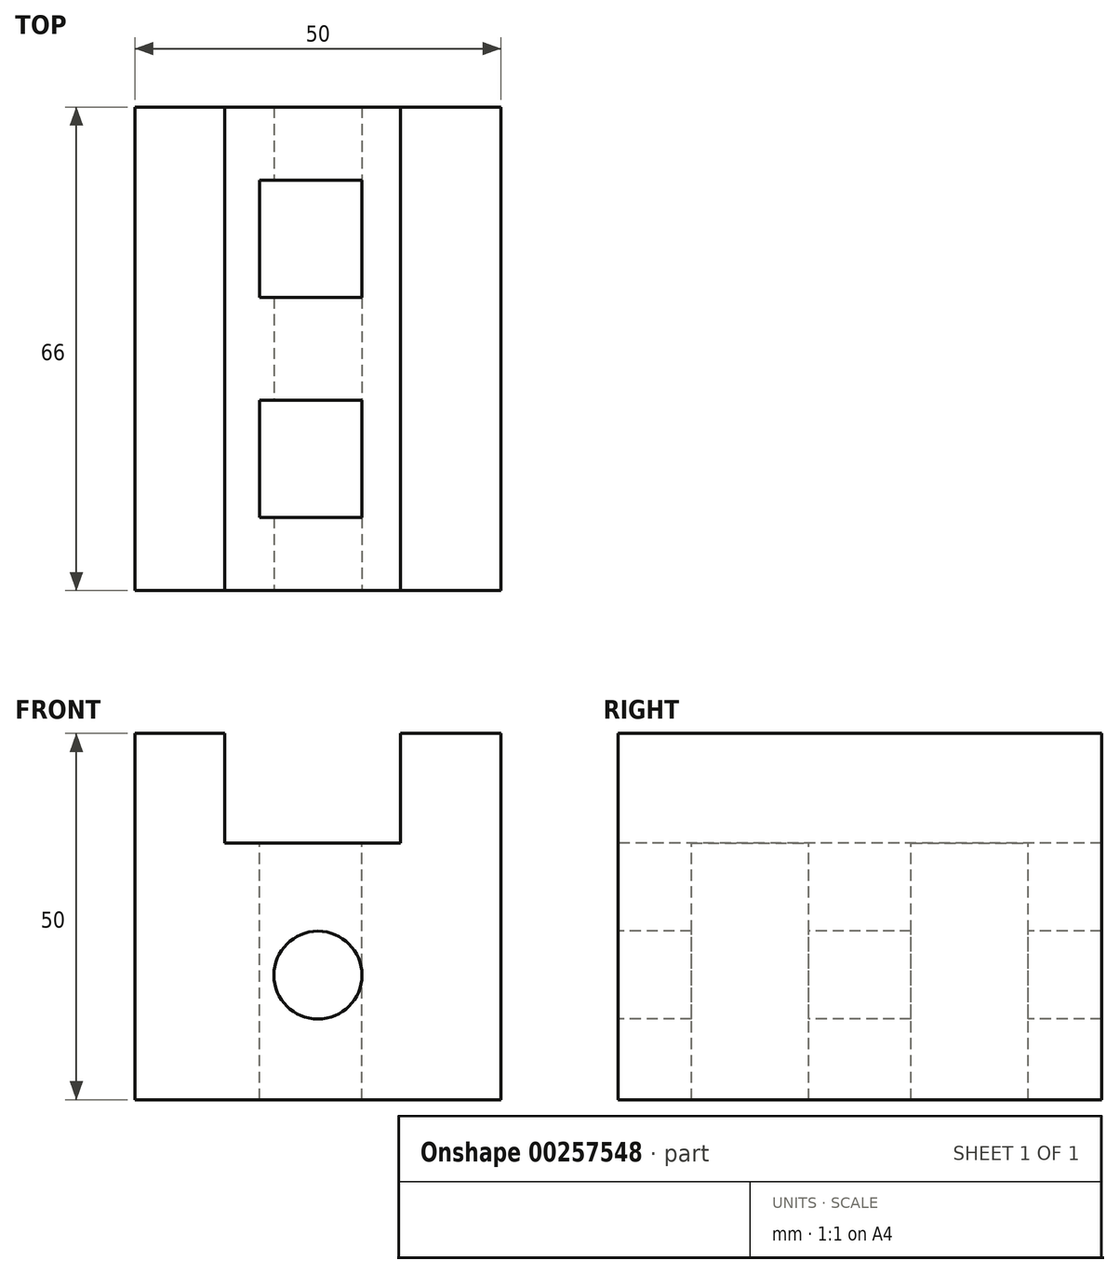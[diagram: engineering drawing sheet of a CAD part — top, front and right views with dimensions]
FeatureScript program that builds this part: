
annotation { "Feature Type Name" : "Feature", "Feature Type Description" : "" }
export const myFeature = defineFeature(function(context is Context, id is Id, definition is map)
    precondition{}
    {
        {
            var Q0;
            Q0=qCreatedBy(makeId("Top.planeOp"),FACE);
            var sketch = newSketch(context, id + "F0", { "sketchPlane" : qUnion([Q0])});
            skLineSegment(sketch, "E0.bottom", {"start": v(25, 33) * mm, "end": v(-25, 33) * mm});
            skLineSegment(sketch, "E0.top", {"start": v(25, -33) * mm, "end": v(-25, -33) * mm});
            skLineSegment(sketch, "E0.left", {"start": v(25, 33) * mm, "end": v(25, -33) * mm});
            skLineSegment(sketch, "E0.right", {"start": v(-25, 33) * mm, "end": v(-25, -33) * mm});
            skPoint(sketch, "E0.middle", {"position": v(0, 0) * mm});
            skSolve(sketch);
        }
        {
            var Q0;
            Q0=makeQuery(id+"F0.imprint","IMPRINT",FACE,{"disambiguationData":[TD([[makeQuery(id+"F0.imprint","IMPRINT",EDGE,{"derivedFrom":sQuery(id+"F0.wireOp",EDGE,"E0.bottom")}),1.0]])]});
            extrude(context, id + "F1", {"entities" : qUnion([Q0]), "oppositeDirection" : true, "depth" : 50 * mm});
        }
        {
            var Q0;
            Q0=makeQuery(id+"F1.opExtrude","SWEPT_FACE",FACE,{"disambiguationData":[OSD([sQuery(id+"F0.wireOp",EDGE,"E0.top")])]});
            var sketch = newSketch(context, id + "F2", { "sketchPlane" : qUnion([Q0])});
            skLineSegment(sketch, "E1", {"start": v(-12.73, 0) * mm, "end": v(-12.73, -15) * mm});
            skLineSegment(sketch, "E2", {"start": v(-12.73, -15) * mm, "end": v(11.27, -15) * mm});
            skLineSegment(sketch, "E3", {"start": v(11.27, 0) * mm, "end": v(11.27, -15) * mm});
            skSolve(sketch);
        }
        {
            var Q0;
            {var subQ0=sQuery(id+"F2.wireOp",EDGE,"E1");Q0=makeQuery(id+"F2.imprint","IMPRINT",FACE,{"disambiguationData":[TD([[makeQuery(id+"F2.imprint","IMPRINT",EDGE,{"derivedFrom":subQ0}),1.0]])]});}
            extrude(context, id + "F3", {"entities" : qUnion([Q0]), "operationType" : NewBodyOperationType.REMOVE, "oppositeDirection" : true, "depth" : 100 * mm});
        }
        {
            var Q0;
            Q0=makeQuery(id+"F1.opExtrude","SWEPT_FACE",FACE,{"disambiguationData":[OSD([sQuery(id+"F0.wireOp",EDGE,"E0.top")])]});
            var sketch = newSketch(context, id + "F4", { "sketchPlane" : qUnion([Q0])});
            skLineSegment(sketch, "E4", {"start": v(-25, -50) * mm, "end": v(0, -50) * mm});
            skLineSegment(sketch, "E5", {"start": v(0, -50) * mm, "end": v(0, -33) * mm});
            skCircle(sketch, "E6", {"center": v(0, -33) * mm, "radius": 6 * mm});
            skSolve(sketch);
        }
        {
            var Q0;
            Q0=makeQuery(id+"F4.imprint","IMPRINT",FACE,{"disambiguationData":[TD([[makeQuery(id+"F4.imprint","IMPRINT",EDGE,{"derivedFrom":sQuery(id+"F4.wireOp",EDGE,"E6")}),1.0]])]});
            extrude(context, id + "F5", {"entities" : qUnion([Q0]), "operationType" : NewBodyOperationType.REMOVE, "oppositeDirection" : true, "depth" : 100 * mm});
        }
        {
            var Q0;
            Q0=makeQuery(id+"F3.boolean.opBoolean","COPY",FACE,{"derivedFrom":makeQuery(id+"F3.opExtrude","SWEPT_FACE",FACE,{"disambiguationData":[OSD([sQuery(id+"F2.wireOp",EDGE,"E2")])]})});
            var sketch = newSketch(context, id + "F6", { "sketchPlane" : qUnion([Q0])});
            skLineSegment(sketch, "E7", {"start": v(-8, 33) * mm, "end": v(-8, 23) * mm});
            skLineSegment(sketch, "E8", {"start": v(-8, 7) * mm, "end": v(-8, 23) * mm});
            skLineSegment(sketch, "E9", {"start": v(-8, 7) * mm, "end": v(-8, -7) * mm});
            skLineSegment(sketch, "E10", {"start": v(-8, -23) * mm, "end": v(-8, -7) * mm});
            skLineSegment(sketch, "E11", {"start": v(-8, -23) * mm, "end": v(-8, -33) * mm});
            skLineSegment(sketch, "E12.bottom", {"start": v(-8, -23) * mm, "end": v(6, -23) * mm});
            skLineSegment(sketch, "E12.top", {"start": v(-8, -7) * mm, "end": v(6, -7) * mm});
            skLineSegment(sketch, "E12.right", {"start": v(6, -23) * mm, "end": v(6, -7) * mm});
            skLineSegment(sketch, "E13.bottom", {"start": v(-8, 7) * mm, "end": v(6, 7) * mm});
            skLineSegment(sketch, "E13.top", {"start": v(-8, 23) * mm, "end": v(6, 23) * mm});
            skLineSegment(sketch, "E13.right", {"start": v(6, 7) * mm, "end": v(6, 23) * mm});
            skSolve(sketch);
        }
        {
            var Q0;
            Q0=makeQuery(id+"F6.imprint","IMPRINT",FACE,{"disambiguationData":[TD([[makeQuery(id+"F6.imprint","IMPRINT",EDGE,{"derivedFrom":sQuery(id+"F6.wireOp",EDGE,"E13.bottom")}),1.0]])]});
            var Q1;
            Q1=makeQuery(id+"F6.imprint","IMPRINT",FACE,{"disambiguationData":[TD([[makeQuery(id+"F6.imprint","IMPRINT",EDGE,{"derivedFrom":sQuery(id+"F6.wireOp",EDGE,"E12.bottom")}),1.0]])]});
            extrude(context, id + "F7", {"entities" : qUnion([Q0, Q1]), "operationType" : NewBodyOperationType.REMOVE, "oppositeDirection" : true, "depth" : 100 * mm});
        }
    });
